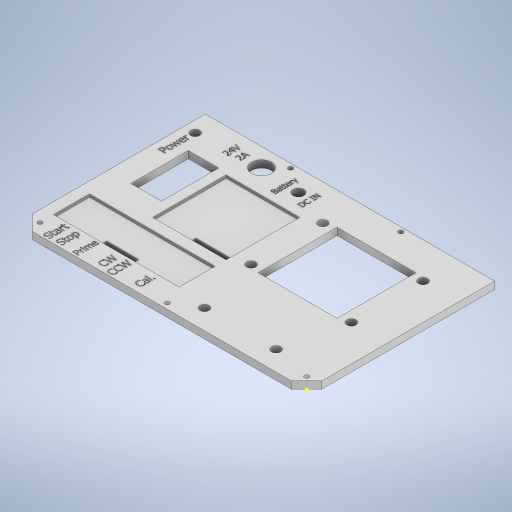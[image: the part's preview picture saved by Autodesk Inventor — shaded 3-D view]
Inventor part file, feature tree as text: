
AUTODESK INVENTOR PART (.ipt)
format: ipt  version: 2023 (Build 270158000, 158)  size: 1,841,152 bytes
history: native  units: in
note: dims shown in document units (in); Inventor stores cm internally (conversion verified against a paired STEP export)
features: extrude x9, sketch x9, other x2, chamfer x1, projected_geometry x1
ambient origin geometry x8: Origin, YZ Plane, XZ Plane, XY Plane, X Axis, Y Axis, Z Axis, Center Point
bodies: Solid1 (feature_tree)
feature tree (22):
  extrude  "Extrusion1"  Depth=4.1339in
  sketch  "Sketch2"  dims[d2=0.1575in d3=0.0in d4=0.6693in]
  extrude  "Extrusion2"  Depth=0.6693in
  sketch  "Sketch3"  dims[d5=1.2598in d12=0.8988in]
  extrude  "Extrusion3"  Depth=1.2598in
  extrude  "Extrusion4"  Depth=0.1181in
  extrude  "Extrusion5"  Depth=0.013in
  chamfer  "Chamfer1"  Distance=1.6142in
  sketch  "Sketch5"  dims[d39=0.3077in d40=0.013in]
  extrude  "Extrusion8"  Depth=1.6142in
  extrude  "Extrusion10"  Depth=0.7874in
  extrude  "Extrusion11"  Depth=0.7874in
  extrude  "Extrusion12"  Depth=0.7874in
  sketch  "Sketch1"  dims[d0=6.3583in d1=4.1339in]
  other  "Image1"
  sketch  "Sketch4"  dims[d13=2.0131in d30=0.1181in]
  sketch  "Sketch8"  dims[d42=0.0135in]
  sketch  "Sketch10"  dims[d44=0.2153in]
  sketch  "Sketch11"  dims[d47=2.7559in]
  other  "Image3"
  projected_geometry  "Projected Loop1"
  sketch  "Sketch12"  dims[d48=0.7874in d50=1.6142in d51=1.6142in d53=2.8346in d54=2.6378in d56=0.1969in d57=0.1969in d58=0.6299in d59=0.6299in d60=0.8661in d68=0.4331in d71=0.2362in d74=0.1969in d75=0.2008in d76=0.3543in d82=0.1575in d83=0.0in d84=0.0591in d85=0.0in d86=0.0591in d87=0.0in d88=0.7087in d89=0.1378in d90=1.0236in d91=0.748in d92=0.1378in d93=0.0in d94=0.0in d95=0.3346in d96=0.0787in d97=45.0deg d119=0.0984in d120=0.1181in d121=0.0984in d123=0.0984in d127=1.9685in d128=0.3937in d129=0.0in d132=0.1969in d133=0.4724in d135=1.9685in d140=0.1181in d141=0.4733in d142=0.2366in d143=6.3583in d144=3.1791in d145=0.1181in d146=0.4733in d147=0.2366in d148=0.1969in d149=0.0984in d150=0.0984in d151=0.0984in d155=0.4724in d156=0.5512in d157=1.7323in d158=1.7323in d159=0.5512in d161=0.3937in d162=0.1969in d163=0.7874in d165=2.2047in d166=0.7874in d168=1.5748in d171=0.7874in d172=1.1024in d173=0.1575in d174=0.0in d187=0.9055in d198=0.0984in d199=0.0in d200=0.0709in d201=0.0709in d202=0.0709in d203=0.0709in d206=0.0177in d207=0.0984in d208=0.0in d209=0.0709in d210=0.7874in d212=0.5in d213=0.7874in d215=0.8in]
